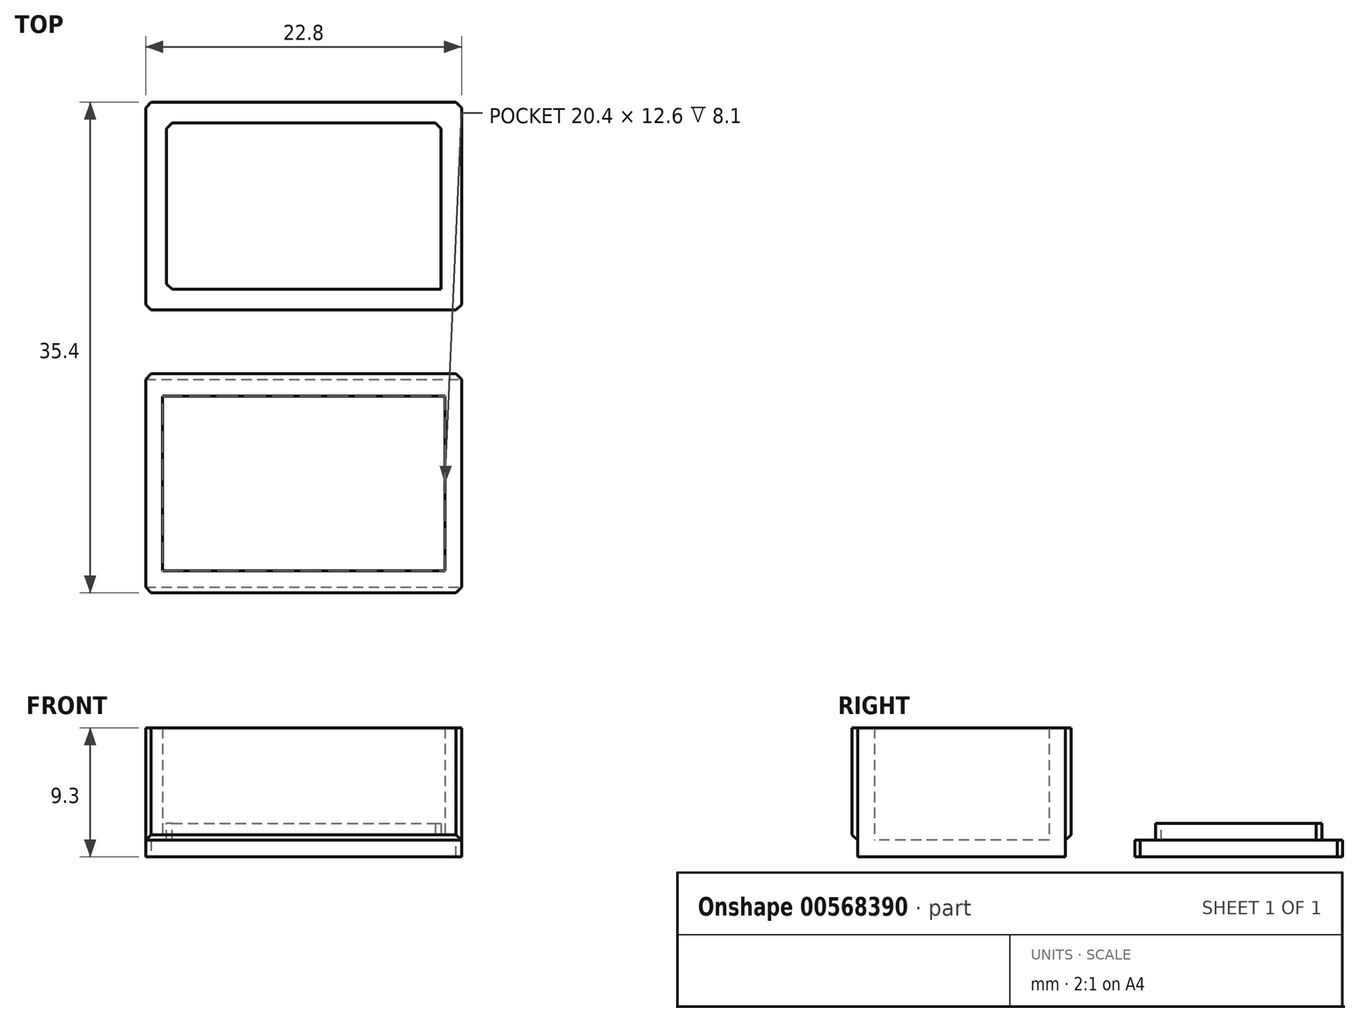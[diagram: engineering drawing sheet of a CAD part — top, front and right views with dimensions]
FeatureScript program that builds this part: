
annotation { "Feature Type Name" : "Feature", "Feature Type Description" : "" }
export const myFeature = defineFeature(function(context is Context, id is Id, definition is map)
    precondition{}
    {
        {
            var Q0;
            Q0=qCreatedBy(makeId("Top.planeOp"),FACE);
            var sketch = newSketch(context, id + "F0", { "sketchPlane" : qUnion([Q0])});
            skLineSegment(sketch, "E0.bottom", {"start": v(-11.4, 7.5) * mm, "end": v(11.4, 7.5) * mm});
            skLineSegment(sketch, "E0.top", {"start": v(-11.4, -7.5) * mm, "end": v(11.4, -7.5) * mm});
            skLineSegment(sketch, "E0.left", {"start": v(-11.4, 7.5) * mm, "end": v(-11.4, -7.5) * mm});
            skLineSegment(sketch, "E0.right", {"start": v(11.4, 7.5) * mm, "end": v(11.4, -7.5) * mm});
            skPoint(sketch, "E0.middle", {"position": v(0, 0) * mm});
            skLineSegment(sketch, "E1.bottom", {"start": v(11.4, 12.5) * mm, "end": v(-11.4, 12.5) * mm});
            skLineSegment(sketch, "E1.top", {"start": v(11.4, 27.5) * mm, "end": v(-11.4, 27.5) * mm});
            skLineSegment(sketch, "E1.left", {"start": v(11.4, 12.5) * mm, "end": v(11.4, 27.5) * mm});
            skLineSegment(sketch, "E1.right", {"start": v(-11.4, 12.5) * mm, "end": v(-11.4, 27.5) * mm});
            skPoint(sketch, "E1.middle", {"position": v(0, 20) * mm});
            skSolve(sketch);
        }
        {
            var Q0;
            Q0=qSketchRegion(id+"F0",true);
            extrude(context, id + "F1", {"entities" : qUnion([Q0]), "depth" : 1.2 * mm, "offsetDistance" : 25 * mm});
        }
        {
            var Q0;
            Q0=makeQuery(id+"F1.opExtrude","CAP_FACE",FACE,{"disambiguationData":[OSD([sQuery(id+"F0.wireOp",EDGE,"E0.bottom"),sQuery(id+"F0.wireOp",EDGE,"E0.top"),sQuery(id+"F0.wireOp",EDGE,"E0.left"),sQuery(id+"F0.wireOp",EDGE,"E0.right")])],"isStart":false});
            var sketch = newSketch(context, id + "F2", { "sketchPlane" : qUnion([Q0])});
            skLineSegment(sketch, "E2.bottom", {"start": v(-10.2, 6.3) * mm, "end": v(10.2, 6.3) * mm});
            skLineSegment(sketch, "E2.top", {"start": v(-10.2, -6.3) * mm, "end": v(10.2, -6.3) * mm});
            skLineSegment(sketch, "E2.left", {"start": v(-10.2, 6.3) * mm, "end": v(-10.2, -6.3) * mm});
            skLineSegment(sketch, "E2.right", {"start": v(10.2, 6.3) * mm, "end": v(10.2, -6.3) * mm});
            skPoint(sketch, "E2.middle", {"position": v(0, 0) * mm});
            skLineSegment(sketch, "E3.bottom", {"start": v(-11.4, 7.5) * mm, "end": v(11.4, 7.5) * mm});
            skLineSegment(sketch, "E3.top", {"start": v(-11.4, -7.5) * mm, "end": v(11.4, -7.5) * mm});
            skLineSegment(sketch, "E3.left", {"start": v(-11.4, 7.5) * mm, "end": v(-11.4, -7.5) * mm});
            skLineSegment(sketch, "E3.right", {"start": v(11.4, 7.5) * mm, "end": v(11.4, -7.5) * mm});
            skLineSegment(sketch, "E4.bottom", {"start": v(-11.4, 7.9) * mm, "end": v(11.4, 7.9) * mm});
            skLineSegment(sketch, "E4.top", {"start": v(-11.4, -7.9) * mm, "end": v(11.4, -7.9) * mm});
            skLineSegment(sketch, "E4.left", {"start": v(-11.4, 7.9) * mm, "end": v(-11.4, -7.9) * mm});
            skLineSegment(sketch, "E4.right", {"start": v(11.4, 7.9) * mm, "end": v(11.4, -7.9) * mm});
            skSolve(sketch);
        }
        {
            var Q0;
            Q0=qSketchRegion(id+"F2",true);
            extrude(context, id + "F3", {"entities" : qUnion([Q0]), "operationType" : NewBodyOperationType.ADD, "depth" : 8.1 * mm, "offsetDistance" : 25 * mm});
        }
        {
            var Q0;
            Q0=makeQuery(id+"F1.opExtrude","CAP_FACE",FACE,{"disambiguationData":[OSD([sQuery(id+"F0.wireOp",EDGE,"E1.bottom"),sQuery(id+"F0.wireOp",EDGE,"E1.top"),sQuery(id+"F0.wireOp",EDGE,"E1.left"),sQuery(id+"F0.wireOp",EDGE,"E1.right")])],"isStart":false});
            var sketch = newSketch(context, id + "F4", { "sketchPlane" : qUnion([Q0])});
            skLineSegment(sketch, "E5.bottom", {"start": v(-9.9, 26) * mm, "end": v(9.9, 26) * mm});
            skLineSegment(sketch, "E5.top", {"start": v(-9.9, 14) * mm, "end": v(9.9, 14) * mm});
            skLineSegment(sketch, "E5.left", {"start": v(-9.9, 26) * mm, "end": v(-9.9, 14) * mm});
            skLineSegment(sketch, "E5.right", {"start": v(9.9, 26) * mm, "end": v(9.9, 14) * mm});
            skPoint(sketch, "E5.middle", {"position": v(0, 20) * mm});
            skSolve(sketch);
        }
        {
            var Q0;
            Q0=makeQuery(id+"F4.imprint","IMPRINT",FACE,{"disambiguationData":[TD([[makeQuery(id+"F4.imprint","IMPRINT",EDGE,{"derivedFrom":sQuery(id+"F4.wireOp",EDGE,"E5.bottom")}),-1.0]])]});
            extrude(context, id + "F5", {"entities" : qUnion([Q0]), "operationType" : NewBodyOperationType.ADD, "depth" : 1.2 * mm, "offsetDistance" : 25 * mm});
        }
        {
            var Q0;
            Q0=makeQuery(id+"F3.opExtrude","CAP_EDGE",EDGE,{"disambiguationData":[OSD([sQuery(id+"F2.wireOp",EDGE,"E4.top")])],"isStart":true});
            var Q1;
            Q1=makeQuery(id+"F3.opExtrude","SWEPT_EDGE",EDGE,{"disambiguationData":[OSD([sQuery(id+"F2.wireOp",EDGE,"E4.top"),sQuery(id+"F2.wireOp",EDGE,"E4.right")])]});
            var Q2;
            Q2=makeQuery(id+"F3.opExtrude","SWEPT_EDGE",EDGE,{"disambiguationData":[OSD([sQuery(id+"F2.wireOp",EDGE,"E4.top"),sQuery(id+"F2.wireOp",EDGE,"E4.left")])]});
            var Q3;
            Q3=makeQuery(id+"F1.opExtrude","SWEPT_EDGE",EDGE,{"disambiguationData":[OSD([sQuery(id+"F0.wireOp",EDGE,"E1.bottom"),sQuery(id+"F0.wireOp",EDGE,"E1.left")])]});
            var Q4;
            Q4=makeQuery(id+"F1.opExtrude","SWEPT_EDGE",EDGE,{"disambiguationData":[OSD([sQuery(id+"F0.wireOp",EDGE,"E1.bottom"),sQuery(id+"F0.wireOp",EDGE,"E1.right")])]});
            var Q5;
            Q5=makeQuery(id+"F3.opExtrude","SWEPT_EDGE",EDGE,{"disambiguationData":[OSD([sQuery(id+"F2.wireOp",EDGE,"E4.bottom"),sQuery(id+"F2.wireOp",EDGE,"E4.right")])]});
            var Q6;
            Q6=makeQuery(id+"F3.opExtrude","CAP_EDGE",EDGE,{"disambiguationData":[OSD([sQuery(id+"F2.wireOp",EDGE,"E4.bottom")])],"isStart":true});
            var Q7;
            Q7=makeQuery(id+"F3.opExtrude","SWEPT_EDGE",EDGE,{"disambiguationData":[OSD([sQuery(id+"F2.wireOp",EDGE,"E4.bottom"),sQuery(id+"F2.wireOp",EDGE,"E4.left")])]});
            var Q8;
            Q8=makeQuery(id+"F1.opExtrude","SWEPT_EDGE",EDGE,{"disambiguationData":[OSD([sQuery(id+"F0.wireOp",EDGE,"E1.top"),sQuery(id+"F0.wireOp",EDGE,"E1.right")])]});
            var Q9;
            Q9=makeQuery(id+"F5.opExtrude","SWEPT_EDGE",EDGE,{"disambiguationData":[OSD([sQuery(id+"F4.wireOp",EDGE,"E5.bottom"),sQuery(id+"F4.wireOp",EDGE,"E5.left")])]});
            var Q10;
            Q10=makeQuery(id+"F5.opExtrude","SWEPT_EDGE",EDGE,{"disambiguationData":[OSD([sQuery(id+"F4.wireOp",EDGE,"E5.top"),sQuery(id+"F4.wireOp",EDGE,"E5.left")])]});
            var Q11;
            Q11=makeQuery(id+"F1.opExtrude","SWEPT_EDGE",EDGE,{"disambiguationData":[OSD([sQuery(id+"F0.wireOp",EDGE,"E1.top"),sQuery(id+"F0.wireOp",EDGE,"E1.left")])]});
            var Q12;
            Q12=makeQuery(id+"F5.opExtrude","SWEPT_EDGE",EDGE,{"disambiguationData":[OSD([sQuery(id+"F4.wireOp",EDGE,"E5.bottom"),sQuery(id+"F4.wireOp",EDGE,"E5.right")])]});
            chamfer(context, id + "F6", {"entities" : qUnion([Q0, Q1, Q2, Q3, Q4, Q5, Q6, Q7, Q8, Q9, Q10, Q11, Q12]), "width" : .4 * mm, "tangentPropagation" : true});
        }
    });
